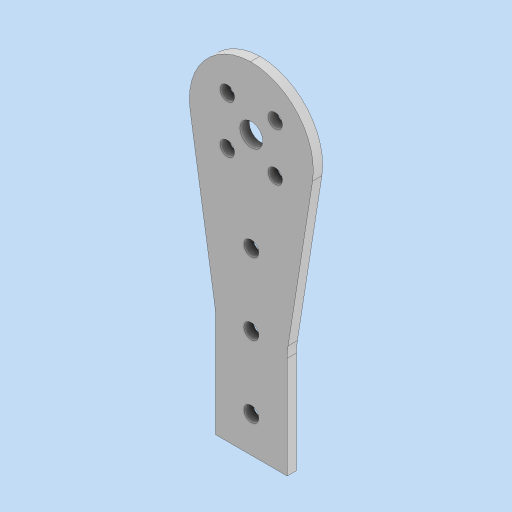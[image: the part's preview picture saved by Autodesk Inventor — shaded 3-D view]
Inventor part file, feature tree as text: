
AUTODESK INVENTOR PART (.ipt)
format: ipt  version: 2024 (Build 280153000, 153)  size: 166,400 bytes
history: native  units: in
note: dims shown in document units (in); Inventor stores cm internally (conversion verified against a paired STEP export)
features: fillet x5, sketch x2, extrude x1, hole x1, pattern_circular x1
ambient origin geometry x8: Origin, YZ Plane, XZ Plane, XY Plane, X Axis, Y Axis, Z Axis, Center Point
bodies: Solid1 (feature_tree)
feature tree (10):
  extrude  "Extrusion1"  Depth=0.875in
  fillet  "Fillet9"  Radius=0.209in
  fillet  "Fillet10"  Radius=0.209in
  fillet  "Fillet11"  Radius=0.875in
  fillet  "Fillet12"  Radius=0.875in
  hole  "Hole1"  [1 undecoded]
  pattern_circular  "Circular Pattern2"  [2 undecoded]
  fillet  "Fillet15"  Radius=0.5in
  sketch  "Sketch1"  dims[d0=1.75in d2=0.3189in d3=0.209in d4=0.209in d5=0.875in d8=0.875in]
  sketch  "Sketch3"  dims[d9=0.875in d10=0.13in d11=0.0in d20=0.5in d21=0.5in d22=0.875in d23=0.875in d26=1.2598in d27=0.6299in d28=0.9449in d29=0.201in d30=0.75in d31=0.37in d32=0.25in d33=90.0deg d34=0.559in d35=0.8108in d40=45.0deg d41=1.5748in d42=360.0deg d44=0.209in d47=1.0in d50=90.0deg d51=1.375in d53=0.5in d54=1.0in d55=1.0in d56=0.0in d16=0.0in d17=0.0in d18=0.0in d19=0.0in]
note: 3 required parameter values undecoded (feature->parameter linkage not recoverable at this tier; creation-order binding heuristic only, values carry confidence <= 0.55)
